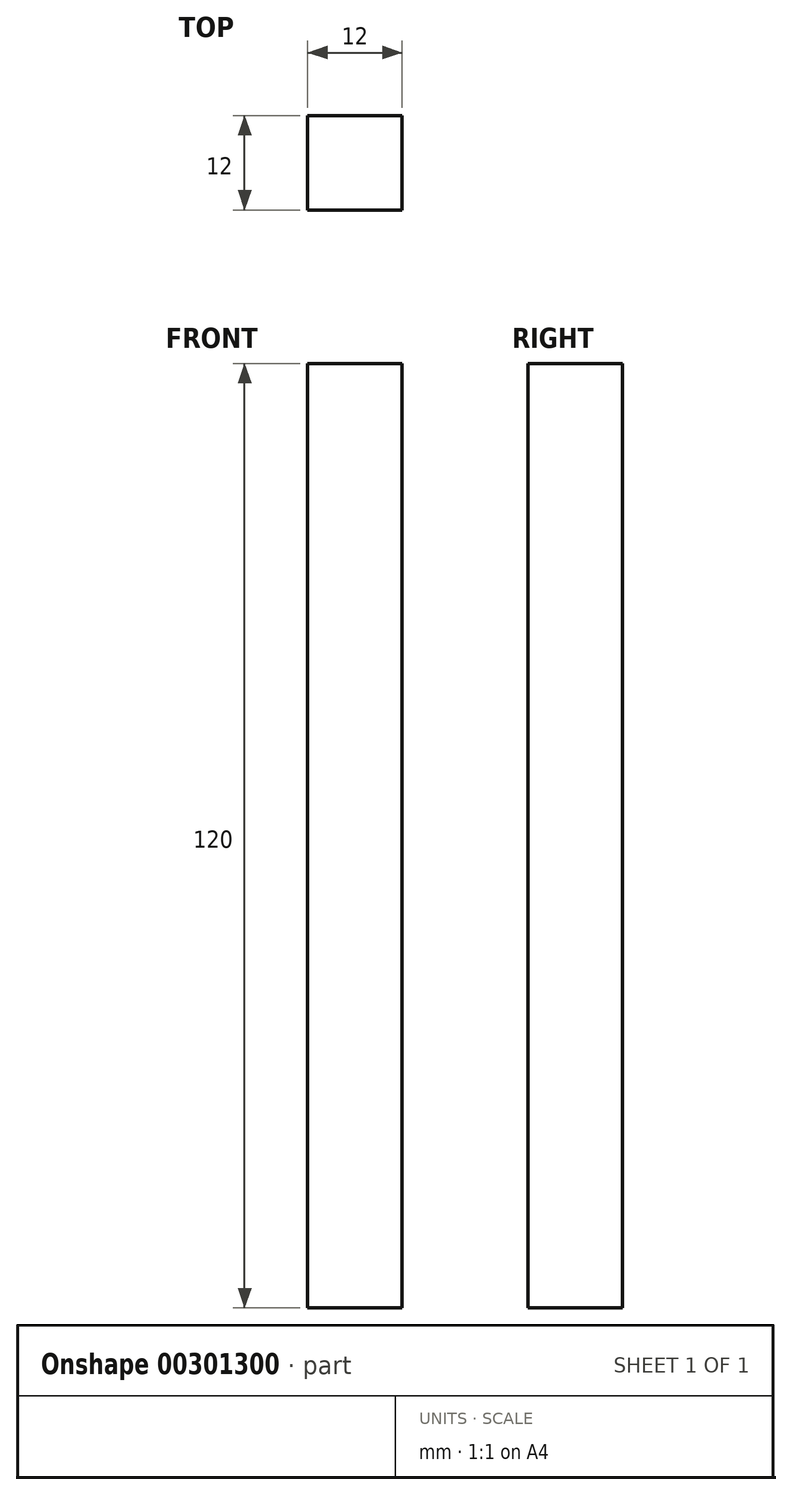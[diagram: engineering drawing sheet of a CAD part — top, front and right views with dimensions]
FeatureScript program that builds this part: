
annotation { "Feature Type Name" : "Feature", "Feature Type Description" : "" }
export const myFeature = defineFeature(function(context is Context, id is Id, definition is map)
    precondition{}
    {
        {
            var Q0;
            Q0=qCreatedBy(makeId("Top.planeOp"),FACE);
            var sketch = newSketch(context, id + "F0", { "sketchPlane" : qUnion([Q0])});
            skLineSegment(sketch, "E0.bottom", {"start": v(0, 0) * mm, "end": v(60, 0) * mm});
            skLineSegment(sketch, "E0.top", {"start": v(0, -60) * mm, "end": v(60, -60) * mm});
            skLineSegment(sketch, "E0.left", {"start": v(0, 0) * mm, "end": v(0, -60) * mm});
            skLineSegment(sketch, "E0.right", {"start": v(60, 0) * mm, "end": v(60, -60) * mm});
            skSolve(sketch);
        }
        {
            var Q0;
            Q0=makeQuery(id+"F0.imprint","IMPRINT",FACE,{"disambiguationData":[TD([[makeQuery(id+"F0.imprint","IMPRINT",EDGE,{"derivedFrom":sQuery(id+"F0.wireOp",EDGE,"E0.bottom")}),-1.0]])]});
            extrude(context, id + "F1", {"entities" : qUnion([Q0]), "oppositeDirection" : true, "depth" : 600 * mm});
        }
        {
            var Q0;
            Q0=makeQuery(id+"F1.opExtrude","SWEPT_BODY",BODY,{"disambiguationData":[OSD([sQuery(id+"F0.wireOp",EDGE,"E0.bottom"),sQuery(id+"F0.wireOp",EDGE,"E0.top"),sQuery(id+"F0.wireOp",EDGE,"E0.left"),sQuery(id+"F0.wireOp",EDGE,"E0.right")])]});
            var Q1;
            Q1=qCreatedBy(makeId("Origin.pointOp"),VERTEX);
            transform(context, id + "F2", {"entities" : qUnion([Q0]), "transformType" : TransformType.SCALE_UNIFORMLY, "scale" : 0.2, "scalePoint" : qUnion([Q1]), "makeCopy" : false});
        }
    });
